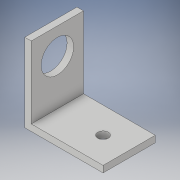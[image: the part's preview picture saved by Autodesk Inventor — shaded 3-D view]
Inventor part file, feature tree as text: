
AUTODESK INVENTOR PART (.ipt)
format: ipt  version: 2018 (Build 220112000, 112)  size: 119,296 bytes
history: native  units: in
note: dims shown in document units (in); Inventor stores cm internally (conversion verified against a paired STEP export)
features: extrude x3, sketch x3
ambient origin geometry x8: Origin, YZ Plane, XZ Plane, XY Plane, X Axis, Y Axis, Z Axis, Center Point
bodies: Solid1 (feature_tree)
feature tree (6):
  extrude  "Extrusion1"  Depth=1.5in
  extrude  "Extrusion2"  Depth=0.125in
  extrude  "Extrusion3"  Depth=1.0in
  sketch  "Sketch1"  dims[d0=0.125in d1=1.5in]
  sketch  "Sketch2"  dims[d2=1.5in d3=0.125in]
  sketch  "Sketch3"  dims[d4=1.0in d5=0.0in d6=1.0in d7=0.6225in d8=1.0in d9=0.0in d10=0.5in d11=180.0deg d12=0.2031in d13=1.0in d14=0.0in]
